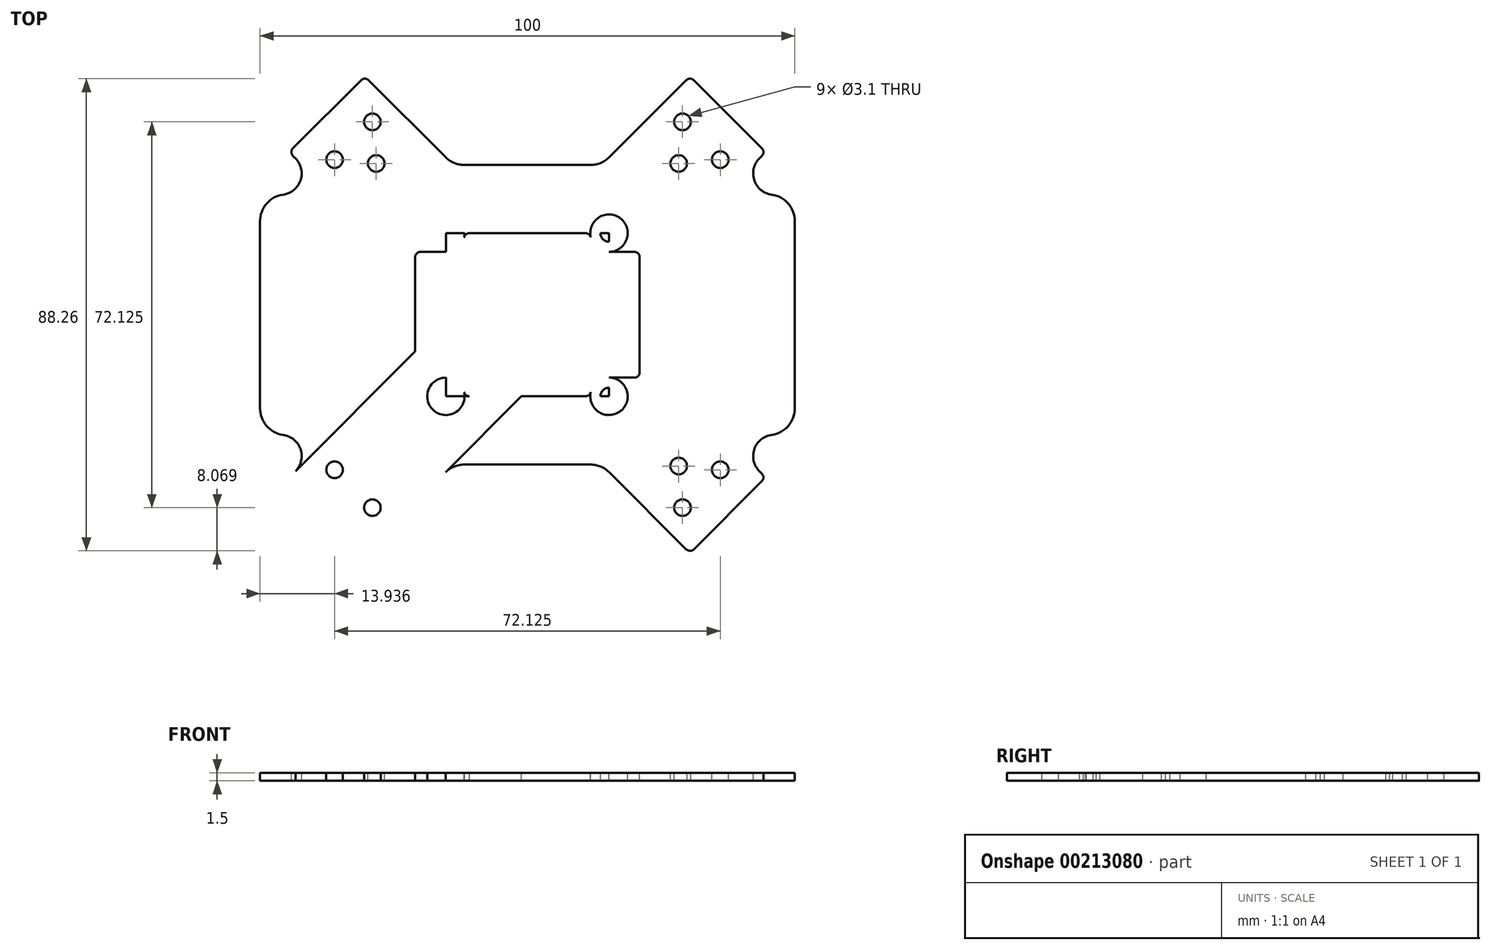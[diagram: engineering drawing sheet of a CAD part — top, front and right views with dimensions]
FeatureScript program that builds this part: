
annotation { "Feature Type Name" : "Feature", "Feature Type Description" : "" }
export const myFeature = defineFeature(function(context is Context, id is Id, definition is map)
    precondition{}
    {
        {
            var Q0;
            Q0=qCreatedBy(makeId("Top.planeOp"),FACE);
            var sketch = newSketch(context, id + "F0", { "sketchPlane" : qUnion([Q0])});
            skLineSegment(sketch, "E0", {"start": v(-118.51, 28.17) * mm, "end": v(21.49, -111.83) * mm});
            skLineSegment(sketch, "E1", {"start": v(-118.51, -111.83) * mm, "end": v(21.49, 28.17) * mm});
            skLineSegment(sketch, "E2", {"start": v(-78.21, 2.01) * mm, "end": v(-4.67, -71.53) * mm});
            skLineSegment(sketch, "E3", {"start": v(-92.35, -12.13) * mm, "end": v(-18.81, -85.67) * mm});
            skLineSegment(sketch, "E4", {"start": v(-30.13, -9.3) * mm, "end": v(-18.81, 2.01) * mm});
            skLineSegment(sketch, "E5", {"start": v(-15.99, -23.44) * mm, "end": v(-4.67, -12.13) * mm});
            skLineSegment(sketch, "E6", {"start": v(-76.51, -27.97) * mm, "end": v(-76.51, -55.69) * mm});
            skLineSegment(sketch, "E7", {"start": v(-20.51, -27.97) * mm, "end": v(-20.51, -55.69) * mm});
            skPoint(sketch, "E8", {"position": v(-48.51, -41.83) * mm});
            skCircle(sketch, "E9", {"center": v(-81.51, -30.04) * mm, "radius": 5 * mm});
            skCircle(sketch, "E10", {"center": v(-81.51, -53.62) * mm, "radius": 5 * mm});
            skCircle(sketch, "E11", {"center": v(-15.51, -30.04) * mm, "radius": 5 * mm});
            skCircle(sketch, "E12", {"center": v(-15.51, -53.62) * mm, "radius": 5 * mm});
            skLineSegment(sketch, "E13", {"start": v(-62.37, -13.83) * mm, "end": v(-34.65, -13.83) * mm});
            skLineSegment(sketch, "E14", {"start": v(-62.37, -69.83) * mm, "end": v(-34.65, -69.83) * mm});
            skCircle(sketch, "E15", {"center": v(-60.3, -74.83) * mm, "radius": 5 * mm});
            skCircle(sketch, "E16", {"center": v(-36.73, -74.83) * mm, "radius": 5 * mm});
            skLineSegment(sketch, "E17", {"start": v(-80.33, -24.15) * mm, "end": v(-66.19, -10) * mm});
            skCircle(sketch, "E18", {"center": v(-76.8, -13.54) * mm, "radius": 1.55 * mm});
            skCircle(sketch, "E19", {"center": v(-77.5, -5.77) * mm, "radius": 1.55 * mm});
            skCircle(sketch, "E20", {"center": v(-84.57, -12.84) * mm, "radius": 1.55 * mm});
            skLineSegment(sketch, "E21", {"start": v(-92.35, -10.72) * mm, "end": v(-79.62, 2.01) * mm});
            skLineSegment(sketch, "E22", {"start": v(-88.1, -16.37) * mm, "end": v(-73.97, -2.23) * mm});
            skLineSegment(sketch, "E23", {"start": v(-48.51, -27.69) * mm, "end": v(-48.51, -55.97) * mm});
            skLineSegment(sketch, "E24", {"start": v(-62.65, -41.83) * mm, "end": v(-34.37, -41.83) * mm});
            skLineSegment(sketch, "E25.MirrorCS", {"start": v(-17.4, -23.44) * mm, "end": v(-30.13, -10.72) * mm});
            skLineSegment(sketch, "E26.MirrorCS", {"start": v(-4.67, -10.72) * mm, "end": v(-17.4, 2.01) * mm});
            skLineSegment(sketch, "E27.MirrorCS", {"start": v(-8.91, -16.37) * mm, "end": v(-23.06, -2.23) * mm});
            skCircle(sketch, "E28.MirrorC", {"center": v(-19.52, -5.77) * mm, "radius": 1.55 * mm});
            skCircle(sketch, "E29.MirrorC", {"center": v(-20.23, -13.54) * mm, "radius": 1.55 * mm});
            skCircle(sketch, "E30.MirrorC", {"center": v(-12.45, -12.84) * mm, "radius": 1.55 * mm});
            skPoint(sketch, "E31.newPointB", {"position": v(-30.83, -10) * mm});
            skArc(sketch, "E31.filletArc", {"start": v(-30.13, -9.3) * mm, "mid": v(-30.42, -10) * mm, "end": v(-30.13, -10.72) * mm});
            skPoint(sketch, "E32.newPointB", {"position": v(-16.7, -24.15) * mm});
            skArc(sketch, "E32.filletArc", {"start": v(-17.4, -23.44) * mm, "mid": v(-16.7, -23.74) * mm, "end": v(-15.99, -23.44) * mm});
            skLineSegment(sketch, "E33", {"start": v(-30.13, -9.3) * mm, "end": v(-92.35, -71.53) * mm});
            skLineSegment(sketch, "E34", {"start": v(-15.99, -23.44) * mm, "end": v(-78.21, -85.67) * mm});
            skCircle(sketch, "E35.MirrorC", {"center": v(-76.8, -70.11) * mm, "radius": 1.55 * mm});
            skCircle(sketch, "E36.MirrorC", {"center": v(-77.5, -77.9) * mm, "radius": 1.55 * mm});
            skCircle(sketch, "E37.MirrorC", {"center": v(-84.57, -70.82) * mm, "radius": 1.55 * mm});
            skCircle(sketch, "E38.MirrorC", {"center": v(-20.23, -70.11) * mm, "radius": 1.55 * mm});
            skCircle(sketch, "E39.MirrorC", {"center": v(-12.45, -70.82) * mm, "radius": 1.55 * mm});
            skCircle(sketch, "E40.MirrorC", {"center": v(-19.52, -77.9) * mm, "radius": 1.55 * mm});
            skLineSegment(sketch, "E41.MirrorCS", {"start": v(-92.35, -72.94) * mm, "end": v(-79.62, -85.67) * mm});
            skLineSegment(sketch, "E42.MirrorCS", {"start": v(-4.67, -72.94) * mm, "end": v(-17.4, -85.67) * mm});
            skCircle(sketch, "E43", {"center": v(-63.76, -26.58) * mm, "radius": 1.6 * mm});
            skCircle(sketch, "E44", {"center": v(-33.26, -26.58) * mm, "radius": 1.6 * mm});
            skCircle(sketch, "E45", {"center": v(-33.26, -57.08) * mm, "radius": 1.6 * mm});
            skCircle(sketch, "E46", {"center": v(-63.76, -57.08) * mm, "radius": 1.6 * mm});
            skCircle(sketch, "E47", {"center": v(-63.76, -26.58) * mm, "radius": 3.5 * mm});
            skCircle(sketch, "E48", {"center": v(-33.26, -26.58) * mm, "radius": 3.5 * mm});
            skCircle(sketch, "E49", {"center": v(-33.26, -57.08) * mm, "radius": 3.5 * mm});
            skCircle(sketch, "E50", {"center": v(-63.76, -57.08) * mm, "radius": 3.5 * mm});
            skLineSegment(sketch, "E51", {"start": v(-33.26, -26.58) * mm, "end": v(-33.26, -57.08) * mm});
            skLineSegment(sketch, "E52", {"start": v(-33.26, -57.08) * mm, "end": v(-63.76, -57.08) * mm});
            skLineSegment(sketch, "E53", {"start": v(-63.76, -57.08) * mm, "end": v(-63.76, -26.58) * mm});
            skLineSegment(sketch, "E54", {"start": v(-63.76, -26.58) * mm, "end": v(-33.26, -26.58) * mm});
            skPoint(sketch, "E55.newPointB", {"position": v(-97.08, -15.45) * mm});
            skArc(sketch, "E55.filletArc", {"start": v(-78.21, 2.01) * mm, "mid": v(-78.92, 2.3) * mm, "end": v(-79.62, 2.01) * mm});
            skPoint(sketch, "E56.newPointA", {"position": v(-111.23, -29.59) * mm});
            skArc(sketch, "E56.filletArc", {"start": v(-92.35, -10.72) * mm, "mid": v(-92.65, -11.42) * mm, "end": v(-92.35, -12.13) * mm});
            skPoint(sketch, "E57.newPointB", {"position": v(0.06, -15.45) * mm});
            skArc(sketch, "E57.filletArc", {"start": v(-17.4, 2.01) * mm, "mid": v(-18.1, 2.3) * mm, "end": v(-18.81, 2.01) * mm});
            skPoint(sketch, "E58.newPointA", {"position": v(14.2, -29.59) * mm});
            skArc(sketch, "E58.filletArc", {"start": v(-4.67, -12.13) * mm, "mid": v(-4.38, -11.42) * mm, "end": v(-4.67, -10.72) * mm});
            skPoint(sketch, "E59.newPointB", {"position": v(14.2, -54.07) * mm});
            skArc(sketch, "E59.filletArc", {"start": v(-4.67, -72.94) * mm, "mid": v(-4.38, -72.23) * mm, "end": v(-4.67, -71.53) * mm});
            skPoint(sketch, "E60.newPointA", {"position": v(0.06, -68.21) * mm});
            skArc(sketch, "E60.filletArc", {"start": v(-18.81, -85.67) * mm, "mid": v(-18.1, -85.96) * mm, "end": v(-17.4, -85.67) * mm});
            skPoint(sketch, "E61.newPointB", {"position": v(-97.08, -68.21) * mm});
            skArc(sketch, "E61.filletArc", {"start": v(-79.62, -85.67) * mm, "mid": v(-78.92, -85.96) * mm, "end": v(-78.21, -85.67) * mm});
            skPoint(sketch, "E62.newPointA", {"position": v(-111.23, -54.07) * mm});
            skArc(sketch, "E62.filletArc", {"start": v(-92.35, -71.53) * mm, "mid": v(-92.65, -72.23) * mm, "end": v(-92.35, -72.94) * mm});
            skLineSegment(sketch, "E63", {"start": v(-63.76, -30.08) * mm, "end": v(-68.51, -30.08) * mm});
            skLineSegment(sketch, "E64", {"start": v(-69.51, -31.08) * mm, "end": v(-69.51, -52.58) * mm});
            skLineSegment(sketch, "E65", {"start": v(-68.51, -53.58) * mm, "end": v(-63.76, -53.58) * mm});
            skPoint(sketch, "E66.visualSharp", {"position": v(-69.51, -30.08) * mm});
            skArc(sketch, "E66.filletArc", {"start": v(-68.51, -30.08) * mm, "mid": v(-69.22, -30.37) * mm, "end": v(-69.51, -31.08) * mm});
            skPoint(sketch, "E67.visualSharp", {"position": v(-69.51, -53.58) * mm});
            skArc(sketch, "E67.filletArc", {"start": v(-69.51, -52.58) * mm, "mid": v(-69.22, -53.29) * mm, "end": v(-68.51, -53.58) * mm});
            skLineSegment(sketch, "E68.MirrorCS", {"start": v(-33.26, -30.08) * mm, "end": v(-28.51, -30.08) * mm});
            skArc(sketch, "E69.MirrorCS", {"start": v(-28.51, -30.08) * mm, "mid": v(-27.8, -30.37) * mm, "end": v(-27.51, -31.08) * mm});
            skLineSegment(sketch, "E70.MirrorCS", {"start": v(-27.51, -31.08) * mm, "end": v(-27.51, -52.58) * mm});
            skArc(sketch, "E71.MirrorCS", {"start": v(-27.51, -52.58) * mm, "mid": v(-27.8, -53.29) * mm, "end": v(-28.51, -53.58) * mm});
            skLineSegment(sketch, "E72.MirrorCS", {"start": v(-28.51, -53.58) * mm, "end": v(-33.26, -53.58) * mm});
            skCircle(sketch, "E73", {"center": v(-59.37, -56.08) * mm, "radius": 1 * mm});
            skCircle(sketch, "E74", {"center": v(-37.65, -56.08) * mm, "radius": 1 * mm});
            skCircle(sketch, "E75.MirrorC", {"center": v(-59.37, -27.58) * mm, "radius": 1 * mm});
            skCircle(sketch, "E76.MirrorC", {"center": v(-37.65, -27.58) * mm, "radius": 1 * mm});
            skPoint(sketch, "E77.MirrorP", {"position": v(-63.84, -61.83) * mm});
            skPoint(sketch, "E78.MirrorP", {"position": v(-72.84, -61.83) * mm});
            skLineSegment(sketch, "E79.MirrorCS", {"start": v(-63.84, -62.83) * mm, "end": v(-63.84, -62.83) * mm});
            skPoint(sketch, "E80.MirrorP", {"position": v(-63.84, -63.83) * mm});
            skPoint(sketch, "E81.centerSnap0", {"position": v(-48.51, -26.58) * mm});
            skLineSegment(sketch, "E82", {"start": v(-11.87, -19.33) * mm, "end": v(-3.51, -19.33) * mm});
            skLineSegment(sketch, "E83", {"start": v(1.49, -24.33) * mm, "end": v(1.49, -59.33) * mm});
            skLineSegment(sketch, "E84", {"start": v(-3.51, -64.33) * mm, "end": v(-11.87, -64.33) * mm});
            skLineSegment(sketch, "E85", {"start": v(-85.15, -64.33) * mm, "end": v(-93.51, -64.33) * mm});
            skLineSegment(sketch, "E86", {"start": v(-98.51, -59.33) * mm, "end": v(-98.51, -24.33) * mm});
            skLineSegment(sketch, "E87", {"start": v(-93.51, -19.33) * mm, "end": v(-85.15, -19.33) * mm});
            skCircle(sketch, "E88", {"center": v(-94.73, -15.41) * mm, "radius": 4 * mm});
            skCircle(sketch, "E89.MirrorC", {"center": v(-94.73, -68.25) * mm, "radius": 4 * mm});
            skCircle(sketch, "E90.MirrorC", {"center": v(-2.3, -68.25) * mm, "radius": 4 * mm});
            skCircle(sketch, "E91.MirrorC", {"center": v(-2.3, -15.41) * mm, "radius": 4 * mm});
            skCircle(sketch, "E92.MirrorC", {"center": v(-36.73, -8.83) * mm, "radius": 5 * mm});
            skCircle(sketch, "E93.MirrorC", {"center": v(-60.3, -8.83) * mm, "radius": 5 * mm});
            skPoint(sketch, "E94.visualSharp", {"position": v(-98.51, -19.33) * mm});
            skArc(sketch, "E94.filletArc", {"start": v(-93.51, -19.33) * mm, "mid": v(-97.05, -20.8) * mm, "end": v(-98.51, -24.33) * mm});
            skPoint(sketch, "E95.visualSharp", {"position": v(-98.51, -64.33) * mm});
            skArc(sketch, "E95.filletArc", {"start": v(-98.51, -59.33) * mm, "mid": v(-97.05, -62.86) * mm, "end": v(-93.51, -64.33) * mm});
            skPoint(sketch, "E96.visualSharp", {"position": v(1.49, -19.33) * mm});
            skArc(sketch, "E96.filletArc", {"start": v(1.49, -24.33) * mm, "mid": v(0.02, -20.8) * mm, "end": v(-3.51, -19.33) * mm});
            skPoint(sketch, "E97.visualSharp", {"position": v(1.49, -64.33) * mm});
            skArc(sketch, "E97.filletArc", {"start": v(-3.51, -64.33) * mm, "mid": v(0.02, -62.86) * mm, "end": v(1.49, -59.33) * mm});
            skSolve(sketch);
        }
        {
            var Q0;
            {var subQ0=sQuery(id+"F0.wireOp",EDGE,"E34");var subQ1=sQuery(id+"F0.wireOp",EDGE,"E7");var subQ2=makeQuery(id+"F0.imprint","INTERSECT",VERTEX,{"derivedFrom":[subQ1,subQ0]});Q0=makeQuery(id+"F0.imprint","IMPRINT",FACE,{"disambiguationData":[TD([[makeQuery(id+"F0.imprint","IMPRINT",EDGE,{"disambiguationData":[TD([[subQ2,-1.0]])],"derivedFrom":subQ1}),1.0]])]});}
            var Q1;
            {var subQ0=sQuery(id+"F0.wireOp",EDGE,"E34");var subQ1=sQuery(id+"F0.wireOp",EDGE,"E14");var subQ2=makeQuery(id+"F0.imprint","INTERSECT",VERTEX,{"derivedFrom":[subQ1,subQ0]});Q1=makeQuery(id+"F0.imprint","IMPRINT",FACE,{"disambiguationData":[TD([[makeQuery(id+"F0.imprint","IMPRINT",EDGE,{"disambiguationData":[TD([[subQ2,-1.0]])],"derivedFrom":subQ1}),-1.0]])]});}
            var Q2;
            {var subQ1=sQuery(id+"F0.wireOp",EDGE,"E6");var subQ5=sQuery(id+"F0.wireOp",EDGE,"E3");var subQ6=makeQuery(id+"F0.imprint","INTERSECT",VERTEX,{"derivedFrom":[subQ5,subQ1]});Q2=makeQuery(id+"F0.imprint","IMPRINT",FACE,{"disambiguationData":[TD([[makeQuery(id+"F0.imprint","IMPRINT",EDGE,{"disambiguationData":[TD([[subQ6,-1.0]])],"derivedFrom":subQ5}),-1.0]])]});}
            var Q3;
            {var subQ0=sQuery(id+"F0.wireOp",EDGE,"E6");var subQ1=sQuery(id+"F0.wireOp",EDGE,"E3");var subQ2=makeQuery(id+"F0.imprint","INTERSECT",VERTEX,{"derivedFrom":[subQ1,subQ0]});Q3=makeQuery(id+"F0.imprint","IMPRINT",FACE,{"disambiguationData":[TD([[makeQuery(id+"F0.imprint","IMPRINT",EDGE,{"disambiguationData":[TD([[subQ2,1.0]])],"derivedFrom":subQ1}),-1.0]])]});}
            var Q4;
            {var subQ0=sQuery(id+"F0.wireOp",EDGE,"E7");var subQ5=sQuery(id+"F0.wireOp",EDGE,"E2");var subQ6=makeQuery(id+"F0.imprint","INTERSECT",VERTEX,{"derivedFrom":[subQ5,subQ0]});Q4=makeQuery(id+"F0.imprint","IMPRINT",FACE,{"disambiguationData":[TD([[makeQuery(id+"F0.imprint","IMPRINT",EDGE,{"disambiguationData":[TD([[subQ6,1.0]])],"derivedFrom":subQ5}),1.0]])]});}
            var Q5;
            {var subQ0=sQuery(id+"F0.wireOp",EDGE,"E7");var subQ1=sQuery(id+"F0.wireOp",EDGE,"E2");var subQ2=makeQuery(id+"F0.imprint","INTERSECT",VERTEX,{"derivedFrom":[subQ1,subQ0]});Q5=makeQuery(id+"F0.imprint","IMPRINT",FACE,{"disambiguationData":[TD([[makeQuery(id+"F0.imprint","IMPRINT",EDGE,{"disambiguationData":[TD([[subQ2,-1.0]])],"derivedFrom":subQ1}),1.0]])]});}
            var Q6;
            {var subQ0=sQuery(id+"F0.wireOp",EDGE,"E13");Q6=makeQuery(id+"F0.imprint","IMPRINT",FACE,{"disambiguationData":[TD([[makeQuery(id+"F0.imprint","IMPRINT",EDGE,{"derivedFrom":subQ0}),-1.0]])]});}
            var Q7;
            {var subQ0=sQuery(id+"F0.wireOp",EDGE,"E14");var subQ1=sQuery(id+"F0.wireOp",EDGE,"E3");var subQ2=makeQuery(id+"F0.imprint","INTERSECT",VERTEX,{"derivedFrom":[subQ1,subQ0]});Q7=makeQuery(id+"F0.imprint","IMPRINT",FACE,{"disambiguationData":[TD([[makeQuery(id+"F0.imprint","IMPRINT",EDGE,{"disambiguationData":[TD([[subQ2,1.0]])],"derivedFrom":subQ1}),-1.0]])]});}
            var Q8;
            {var subQ0=sQuery(id+"F0.wireOp",EDGE,"E14");var subQ1=sQuery(id+"F0.wireOp",EDGE,"E3");var subQ2=makeQuery(id+"F0.imprint","INTERSECT",VERTEX,{"derivedFrom":[subQ1,subQ0]});Q8=makeQuery(id+"F0.imprint","IMPRINT",FACE,{"disambiguationData":[TD([[makeQuery(id+"F0.imprint","IMPRINT",EDGE,{"disambiguationData":[TD([[subQ2,-1.0]])],"derivedFrom":subQ1}),-1.0]])]});}
            var Q9;
            {var subQ4=sQuery(id+"F0.wireOp",EDGE,"E22");var subQ7=sQuery(id+"F0.wireOp",EDGE,"E0");var subQ10=makeQuery(id+"F0.imprint","INTERSECT",VERTEX,{"derivedFrom":[subQ7,subQ4]});Q9=makeQuery(id+"F0.imprint","IMPRINT",FACE,{"disambiguationData":[TD([[makeQuery(id+"F0.imprint","IMPRINT",EDGE,{"disambiguationData":[TD([[subQ10,-1.0]])],"derivedFrom":subQ7}),-1.0]])]});}
            var Q10;
            {var subQ11=sQuery(id+"F0.wireOp",EDGE,"E56.filletArc");Q10=makeQuery(id+"F0.imprint","IMPRINT",FACE,{"disambiguationData":[TD([[makeQuery(id+"F0.imprint","IMPRINT",EDGE,{"derivedFrom":subQ11}),1.0]])]});}
            var Q11;
            {var subQ0=sQuery(id+"F0.wireOp",EDGE,"E55.filletArc");Q11=makeQuery(id+"F0.imprint","IMPRINT",FACE,{"disambiguationData":[TD([[makeQuery(id+"F0.imprint","IMPRINT",EDGE,{"derivedFrom":subQ0}),1.0]])]});}
            var Q12;
            {var subQ3=sQuery(id+"F0.wireOp",EDGE,"E22");var subQ6=sQuery(id+"F0.wireOp",EDGE,"E0");var subQ9=makeQuery(id+"F0.imprint","INTERSECT",VERTEX,{"derivedFrom":[subQ6,subQ3]});Q12=makeQuery(id+"F0.imprint","IMPRINT",FACE,{"disambiguationData":[TD([[makeQuery(id+"F0.imprint","IMPRINT",EDGE,{"disambiguationData":[TD([[subQ9,-1.0]])],"derivedFrom":subQ6}),1.0]])]});}
            var Q13;
            {var subQ0=sQuery(id+"F0.wireOp",EDGE,"E17");var subQ3=sQuery(id+"F0.wireOp",EDGE,"E0");var subQ4=makeQuery(id+"F0.imprint","INTERSECT",VERTEX,{"derivedFrom":[subQ3,subQ0]});Q13=makeQuery(id+"F0.imprint","IMPRINT",FACE,{"disambiguationData":[TD([[makeQuery(id+"F0.imprint","IMPRINT",EDGE,{"disambiguationData":[TD([[subQ4,-1.0]])],"derivedFrom":subQ3}),1.0]])]});}
            var Q14;
            {var subQ4=sQuery(id+"F0.wireOp",EDGE,"E63");Q14=makeQuery(id+"F0.imprint","IMPRINT",FACE,{"disambiguationData":[TD([[makeQuery(id+"F0.imprint","IMPRINT",EDGE,{"derivedFrom":subQ4}),-1.0]])]});}
            var Q15;
            {var subQ0=sQuery(id+"F0.wireOp",EDGE,"E31.filletArc");Q15=makeQuery(id+"F0.imprint","IMPRINT",FACE,{"disambiguationData":[TD([[makeQuery(id+"F0.imprint","IMPRINT",EDGE,{"derivedFrom":subQ0}),1.0]])]});}
            var Q16;
            {var subQ5=sQuery(id+"F0.wireOp",EDGE,"E57.filletArc");Q16=makeQuery(id+"F0.imprint","IMPRINT",FACE,{"disambiguationData":[TD([[makeQuery(id+"F0.imprint","IMPRINT",EDGE,{"derivedFrom":subQ5}),1.0]])]});}
            var Q17;
            {var subQ0=sQuery(id+"F0.wireOp",EDGE,"E58.filletArc");Q17=makeQuery(id+"F0.imprint","IMPRINT",FACE,{"disambiguationData":[TD([[makeQuery(id+"F0.imprint","IMPRINT",EDGE,{"derivedFrom":subQ0}),1.0]])]});}
            var Q18;
            {var subQ4=sQuery(id+"F0.wireOp",EDGE,"E32.filletArc");Q18=makeQuery(id+"F0.imprint","IMPRINT",FACE,{"disambiguationData":[TD([[makeQuery(id+"F0.imprint","IMPRINT",EDGE,{"derivedFrom":subQ4}),1.0]])]});}
            var Q19;
            {var subQ1=sQuery(id+"F0.wireOp",EDGE,"E31.filletArc");Q19=makeQuery(id+"F0.imprint","IMPRINT",FACE,{"disambiguationData":[TD([[makeQuery(id+"F0.imprint","IMPRINT",EDGE,{"derivedFrom":subQ1}),-1.0]])]});}
            var Q20;
            {var subQ1=sQuery(id+"F0.wireOp",EDGE,"E32.filletArc");Q20=makeQuery(id+"F0.imprint","IMPRINT",FACE,{"disambiguationData":[TD([[makeQuery(id+"F0.imprint","IMPRINT",EDGE,{"derivedFrom":subQ1}),-1.0]])]});}
            var Q21;
            Q21=makeQuery(id+"F0.imprint","IMPRINT",FACE,{"disambiguationData":[TD([[makeQuery(id+"F0.imprint","IMPRINT",EDGE,{"derivedFrom":sQuery(id+"F0.wireOp",EDGE,"E39.MirrorC")}),-1.0]])]});
            var Q22;
            Q22=makeQuery(id+"F0.imprint","IMPRINT",FACE,{"disambiguationData":[TD([[makeQuery(id+"F0.imprint","IMPRINT",EDGE,{"derivedFrom":sQuery(id+"F0.wireOp",EDGE,"E40.MirrorC")}),-1.0]])]});
            var Q23;
            Q23=makeQuery(id+"F0.imprint","IMPRINT",FACE,{"disambiguationData":[TD([[makeQuery(id+"F0.imprint","IMPRINT",EDGE,{"derivedFrom":sQuery(id+"F0.wireOp",EDGE,"E36.MirrorC")}),1.0]])]});
            var Q24;
            Q24=makeQuery(id+"F0.imprint","IMPRINT",FACE,{"disambiguationData":[TD([[makeQuery(id+"F0.imprint","IMPRINT",EDGE,{"derivedFrom":sQuery(id+"F0.wireOp",EDGE,"E37.MirrorC")}),1.0]])]});
            var Q25;
            {var subQ0=sQuery(id+"F0.wireOp",EDGE,"E47");var subQ1=sQuery(id+"F0.wireOp",EDGE,"E0");var subQ2=makeQuery(id+"F0.imprint","INTERSECT",VERTEX,{"disambiguationData":[OD(0.0)],"derivedFrom":[subQ1,subQ0]});Q25=makeQuery(id+"F0.imprint","IMPRINT",FACE,{"disambiguationData":[TD([[makeQuery(id+"F0.imprint","IMPRINT",EDGE,{"disambiguationData":[TD([[subQ2,-1.0]])],"derivedFrom":subQ1}),-1.0]])]});}
            var Q26;
            {var subQ0=sQuery(id+"F0.wireOp",EDGE,"E47");var subQ1=sQuery(id+"F0.wireOp",EDGE,"E0");var subQ2=makeQuery(id+"F0.imprint","INTERSECT",VERTEX,{"disambiguationData":[OD(0.0)],"derivedFrom":[subQ1,subQ0]});Q26=makeQuery(id+"F0.imprint","IMPRINT",FACE,{"disambiguationData":[TD([[makeQuery(id+"F0.imprint","IMPRINT",EDGE,{"disambiguationData":[TD([[subQ2,-1.0]])],"derivedFrom":subQ1}),1.0]])]});}
            var Q27;
            {var subQ4=sQuery(id+"F0.wireOp",EDGE,"E0");var subQ6=sQuery(id+"F0.wireOp",EDGE,"E43");var subQ7=makeQuery(id+"F0.imprint","INTERSECT",VERTEX,{"disambiguationData":[OD(1.0)],"derivedFrom":[subQ4,subQ6]});Q27=makeQuery(id+"F0.imprint","IMPRINT",FACE,{"disambiguationData":[TD([[makeQuery(id+"F0.imprint","IMPRINT",EDGE,{"disambiguationData":[TD([[subQ7,-1.0]])],"derivedFrom":subQ4}),1.0]])]});}
            var Q28;
            {var subQ0=sQuery(id+"F0.wireOp",EDGE,"E43");var subQ1=sQuery(id+"F0.wireOp",EDGE,"E0");var subQ2=makeQuery(id+"F0.imprint","INTERSECT",VERTEX,{"disambiguationData":[OD(1.0)],"derivedFrom":[subQ1,subQ0]});Q28=makeQuery(id+"F0.imprint","IMPRINT",FACE,{"disambiguationData":[TD([[makeQuery(id+"F0.imprint","IMPRINT",EDGE,{"disambiguationData":[TD([[subQ2,-1.0]])],"derivedFrom":subQ1}),-1.0]])]});}
            var Q29;
            {var subQ0=sQuery(id+"F0.wireOp",EDGE,"E48");var subQ1=sQuery(id+"F0.wireOp",EDGE,"E1");var subQ2=makeQuery(id+"F0.imprint","INTERSECT",VERTEX,{"disambiguationData":[OD(0.0)],"derivedFrom":[subQ1,subQ0]});Q29=makeQuery(id+"F0.imprint","IMPRINT",FACE,{"disambiguationData":[TD([[makeQuery(id+"F0.imprint","IMPRINT",EDGE,{"disambiguationData":[TD([[subQ2,-1.0]])],"derivedFrom":subQ1}),1.0]])]});}
            var Q30;
            {var subQ0=sQuery(id+"F0.wireOp",EDGE,"E48");var subQ1=sQuery(id+"F0.wireOp",EDGE,"E1");var subQ2=makeQuery(id+"F0.imprint","INTERSECT",VERTEX,{"disambiguationData":[OD(0.0)],"derivedFrom":[subQ1,subQ0]});Q30=makeQuery(id+"F0.imprint","IMPRINT",FACE,{"disambiguationData":[TD([[makeQuery(id+"F0.imprint","IMPRINT",EDGE,{"disambiguationData":[TD([[subQ2,-1.0]])],"derivedFrom":subQ1}),-1.0]])]});}
            var Q31;
            {var subQ0=sQuery(id+"F0.wireOp",EDGE,"E44");var subQ1=sQuery(id+"F0.wireOp",EDGE,"E1");var subQ2=makeQuery(id+"F0.imprint","INTERSECT",VERTEX,{"disambiguationData":[OD(1.0)],"derivedFrom":[subQ1,subQ0]});Q31=makeQuery(id+"F0.imprint","IMPRINT",FACE,{"disambiguationData":[TD([[makeQuery(id+"F0.imprint","IMPRINT",EDGE,{"disambiguationData":[TD([[subQ2,-1.0]])],"derivedFrom":subQ1}),-1.0]])]});}
            var Q32;
            {var subQ0=sQuery(id+"F0.wireOp",EDGE,"E44");var subQ1=sQuery(id+"F0.wireOp",EDGE,"E1");var subQ2=makeQuery(id+"F0.imprint","INTERSECT",VERTEX,{"disambiguationData":[OD(1.0)],"derivedFrom":[subQ1,subQ0]});Q32=makeQuery(id+"F0.imprint","IMPRINT",FACE,{"disambiguationData":[TD([[makeQuery(id+"F0.imprint","IMPRINT",EDGE,{"disambiguationData":[TD([[subQ2,-1.0]])],"derivedFrom":subQ1}),1.0]])]});}
            var Q33;
            {var subQ1=sQuery(id+"F0.wireOp",EDGE,"E0");var subQ5=sQuery(id+"F0.wireOp",EDGE,"E49");var subQ6=makeQuery(id+"F0.imprint","INTERSECT",VERTEX,{"disambiguationData":[OD(0.0)],"derivedFrom":[subQ1,subQ5]});Q33=makeQuery(id+"F0.imprint","IMPRINT",FACE,{"disambiguationData":[TD([[makeQuery(id+"F0.imprint","IMPRINT",EDGE,{"disambiguationData":[TD([[subQ6,-1.0]])],"derivedFrom":subQ1}),-1.0]])]});}
            var Q34;
            {var subQ0=sQuery(id+"F0.wireOp",EDGE,"E49");var subQ1=sQuery(id+"F0.wireOp",EDGE,"E0");var subQ2=makeQuery(id+"F0.imprint","INTERSECT",VERTEX,{"disambiguationData":[OD(0.0)],"derivedFrom":[subQ1,subQ0]});Q34=makeQuery(id+"F0.imprint","IMPRINT",FACE,{"disambiguationData":[TD([[makeQuery(id+"F0.imprint","IMPRINT",EDGE,{"disambiguationData":[TD([[subQ2,-1.0]])],"derivedFrom":subQ1}),1.0]])]});}
            var Q35;
            {var subQ0=sQuery(id+"F0.wireOp",EDGE,"E45");var subQ1=sQuery(id+"F0.wireOp",EDGE,"E0");var subQ2=makeQuery(id+"F0.imprint","INTERSECT",VERTEX,{"disambiguationData":[OD(1.0)],"derivedFrom":[subQ1,subQ0]});Q35=makeQuery(id+"F0.imprint","IMPRINT",FACE,{"disambiguationData":[TD([[makeQuery(id+"F0.imprint","IMPRINT",EDGE,{"disambiguationData":[TD([[subQ2,-1.0]])],"derivedFrom":subQ1}),1.0]])]});}
            var Q36;
            {var subQ0=sQuery(id+"F0.wireOp",EDGE,"E45");var subQ1=sQuery(id+"F0.wireOp",EDGE,"E0");var subQ2=makeQuery(id+"F0.imprint","INTERSECT",VERTEX,{"disambiguationData":[OD(1.0)],"derivedFrom":[subQ1,subQ0]});Q36=makeQuery(id+"F0.imprint","IMPRINT",FACE,{"disambiguationData":[TD([[makeQuery(id+"F0.imprint","IMPRINT",EDGE,{"disambiguationData":[TD([[subQ2,-1.0]])],"derivedFrom":subQ1}),-1.0]])]});}
            var Q37;
            {var subQ0=sQuery(id+"F0.wireOp",EDGE,"E50");var subQ1=sQuery(id+"F0.wireOp",EDGE,"E1");var subQ2=makeQuery(id+"F0.imprint","INTERSECT",VERTEX,{"disambiguationData":[OD(0.0)],"derivedFrom":[subQ1,subQ0]});Q37=makeQuery(id+"F0.imprint","IMPRINT",FACE,{"disambiguationData":[TD([[makeQuery(id+"F0.imprint","IMPRINT",EDGE,{"disambiguationData":[TD([[subQ2,-1.0]])],"derivedFrom":subQ1}),-1.0]])]});}
            var Q38;
            {var subQ0=sQuery(id+"F0.wireOp",EDGE,"E50");var subQ1=sQuery(id+"F0.wireOp",EDGE,"E1");var subQ2=makeQuery(id+"F0.imprint","INTERSECT",VERTEX,{"disambiguationData":[OD(0.0)],"derivedFrom":[subQ1,subQ0]});Q38=makeQuery(id+"F0.imprint","IMPRINT",FACE,{"disambiguationData":[TD([[makeQuery(id+"F0.imprint","IMPRINT",EDGE,{"disambiguationData":[TD([[subQ2,-1.0]])],"derivedFrom":subQ1}),1.0]])]});}
            var Q39;
            {var subQ0=sQuery(id+"F0.wireOp",EDGE,"E46");var subQ1=sQuery(id+"F0.wireOp",EDGE,"E1");var subQ2=makeQuery(id+"F0.imprint","INTERSECT",VERTEX,{"disambiguationData":[OD(1.0)],"derivedFrom":[subQ1,subQ0]});Q39=makeQuery(id+"F0.imprint","IMPRINT",FACE,{"disambiguationData":[TD([[makeQuery(id+"F0.imprint","IMPRINT",EDGE,{"disambiguationData":[TD([[subQ2,-1.0]])],"derivedFrom":subQ1}),1.0]])]});}
            var Q40;
            {var subQ0=sQuery(id+"F0.wireOp",EDGE,"E46");var subQ1=sQuery(id+"F0.wireOp",EDGE,"E1");var subQ2=makeQuery(id+"F0.imprint","INTERSECT",VERTEX,{"disambiguationData":[OD(1.0)],"derivedFrom":[subQ1,subQ0]});Q40=makeQuery(id+"F0.imprint","IMPRINT",FACE,{"disambiguationData":[TD([[makeQuery(id+"F0.imprint","IMPRINT",EDGE,{"disambiguationData":[TD([[subQ2,-1.0]])],"derivedFrom":subQ1}),-1.0]])]});}
            var Q41;
            {var subQ0=sQuery(id+"F0.wireOp",EDGE,"E34");var subQ1=sQuery(id+"F0.wireOp",EDGE,"E7");var subQ2=makeQuery(id+"F0.imprint","INTERSECT",VERTEX,{"derivedFrom":[subQ1,subQ0]});Q41=makeQuery(id+"F0.imprint","IMPRINT",FACE,{"disambiguationData":[TD([[makeQuery(id+"F0.imprint","IMPRINT",EDGE,{"disambiguationData":[TD([[subQ2,-1.0]])],"derivedFrom":subQ1}),1.0]])]});}
            var Q42;
            {var subQ0=sQuery(id+"F0.wireOp",EDGE,"E33");var subQ1=sQuery(id+"F0.wireOp",EDGE,"E6");var subQ2=makeQuery(id+"F0.imprint","INTERSECT",VERTEX,{"derivedFrom":[subQ1,subQ0]});Q42=makeQuery(id+"F0.imprint","IMPRINT",FACE,{"disambiguationData":[TD([[makeQuery(id+"F0.imprint","IMPRINT",EDGE,{"disambiguationData":[TD([[subQ2,1.0]])],"derivedFrom":subQ1}),-1.0]])]});}
            var Q43;
            {var subQ0=sQuery(id+"F0.wireOp",EDGE,"E34");var subQ1=sQuery(id+"F0.wireOp",EDGE,"E14");var subQ2=makeQuery(id+"F0.imprint","INTERSECT",VERTEX,{"derivedFrom":[subQ1,subQ0]});Q43=makeQuery(id+"F0.imprint","IMPRINT",FACE,{"disambiguationData":[TD([[makeQuery(id+"F0.imprint","IMPRINT",EDGE,{"disambiguationData":[TD([[subQ2,-1.0]])],"derivedFrom":subQ1}),-1.0]])]});}
            var Q44;
            {var subQ0=sQuery(id+"F0.wireOp",EDGE,"E54");var subQ1=sQuery(id+"F0.wireOp",EDGE,"E47");var subQ2=makeQuery(id+"F0.imprint","INTERSECT",VERTEX,{"derivedFrom":[subQ1,subQ0]});Q44=makeQuery(id+"F0.imprint","IMPRINT",FACE,{"disambiguationData":[TD([[makeQuery(id+"F0.imprint","IMPRINT",EDGE,{"disambiguationData":[TD([[subQ2,1.0]])],"derivedFrom":subQ1}),-1.0]])]});}
            var Q45;
            {var subQ0=sQuery(id+"F0.wireOp",EDGE,"E54");var subQ1=sQuery(id+"F0.wireOp",EDGE,"E48");var subQ2=makeQuery(id+"F0.imprint","INTERSECT",VERTEX,{"derivedFrom":[subQ1,subQ0]});Q45=makeQuery(id+"F0.imprint","IMPRINT",FACE,{"disambiguationData":[TD([[makeQuery(id+"F0.imprint","IMPRINT",EDGE,{"disambiguationData":[TD([[subQ2,-1.0]])],"derivedFrom":subQ1}),-1.0]])]});}
            var Q46;
            {var subQ0=sQuery(id+"F0.wireOp",EDGE,"E74");var subQ1=sQuery(id+"F0.wireOp",EDGE,"E49");var subQ2=makeQuery(id+"F0.imprint","INTERSECT",VERTEX,{"derivedFrom":[subQ1,subQ0]});Q46=makeQuery(id+"F0.imprint","IMPRINT",FACE,{"disambiguationData":[TD([[makeQuery(id+"F0.imprint","IMPRINT",EDGE,{"disambiguationData":[TD([[subQ2,-1.0]])],"derivedFrom":subQ1}),-1.0]])]});}
            var Q47;
            {var subQ0=sQuery(id+"F0.wireOp",EDGE,"E73");var subQ1=sQuery(id+"F0.wireOp",EDGE,"E50");var subQ2=makeQuery(id+"F0.imprint","INTERSECT",VERTEX,{"derivedFrom":[subQ1,subQ0]});Q47=makeQuery(id+"F0.imprint","IMPRINT",FACE,{"disambiguationData":[TD([[makeQuery(id+"F0.imprint","IMPRINT",EDGE,{"disambiguationData":[TD([[subQ2,1.0]])],"derivedFrom":subQ1}),-1.0]])]});}
            var Q48;
            {var subQ0=sQuery(id+"F0.wireOp",EDGE,"E3");var subQ1=makeQuery(id+"F0.imprint","INTERSECT",VERTEX,{"derivedFrom":[subQ0,sQuery(id+"F0.wireOp",EDGE,"E22")]});Q48=makeQuery(id+"F0.imprint","IMPRINT",FACE,{"disambiguationData":[TD([[makeQuery(id+"F0.imprint","IMPRINT",EDGE,{"disambiguationData":[TD([[subQ1,1.0]])],"derivedFrom":subQ0}),-1.0]])]});}
            var Q49;
            {var subQ1=sQuery(id+"F0.wireOp",EDGE,"E86");Q49=makeQuery(id+"F0.imprint","IMPRINT",FACE,{"disambiguationData":[TD([[makeQuery(id+"F0.imprint","IMPRINT",EDGE,{"derivedFrom":subQ1}),-1.0]])]});}
            var Q50;
            {var subQ0=sQuery(id+"F0.wireOp",EDGE,"E10");var subQ1=makeQuery(id+"F0.imprint","INTERSECT",VERTEX,{"derivedFrom":[sQuery(id+"F0.wireOp",EDGE,"E6"),subQ0]});Q50=makeQuery(id+"F0.imprint","IMPRINT",FACE,{"disambiguationData":[TD([[makeQuery(id+"F0.imprint","IMPRINT",EDGE,{"disambiguationData":[TD([[subQ1,-1.0]])],"derivedFrom":subQ0}),1.0]])]});}
            var Q51;
            {var subQ0=sQuery(id+"F0.wireOp",EDGE,"E9");var subQ1=makeQuery(id+"F0.imprint","INTERSECT",VERTEX,{"derivedFrom":[sQuery(id+"F0.wireOp",EDGE,"E3"),subQ0]});Q51=makeQuery(id+"F0.imprint","IMPRINT",FACE,{"disambiguationData":[TD([[makeQuery(id+"F0.imprint","IMPRINT",EDGE,{"disambiguationData":[TD([[subQ1,1.0]])],"derivedFrom":subQ0}),1.0]])]});}
            var Q52;
            {var subQ0=sQuery(id+"F0.wireOp",EDGE,"E83");Q52=makeQuery(id+"F0.imprint","IMPRINT",FACE,{"disambiguationData":[TD([[makeQuery(id+"F0.imprint","IMPRINT",EDGE,{"derivedFrom":subQ0}),-1.0]])]});}
            var Q53;
            {var subQ0=sQuery(id+"F0.wireOp",EDGE,"E11");var subQ1=makeQuery(id+"F0.imprint","INTERSECT",VERTEX,{"derivedFrom":[sQuery(id+"F0.wireOp",EDGE,"E7"),subQ0]});Q53=makeQuery(id+"F0.imprint","IMPRINT",FACE,{"disambiguationData":[TD([[makeQuery(id+"F0.imprint","IMPRINT",EDGE,{"disambiguationData":[TD([[subQ1,1.0]])],"derivedFrom":subQ0}),1.0]])]});}
            var Q54;
            {var subQ0=sQuery(id+"F0.wireOp",EDGE,"E12");var subQ1=makeQuery(id+"F0.imprint","INTERSECT",VERTEX,{"derivedFrom":[sQuery(id+"F0.wireOp",EDGE,"E2"),subQ0]});Q54=makeQuery(id+"F0.imprint","IMPRINT",FACE,{"disambiguationData":[TD([[makeQuery(id+"F0.imprint","IMPRINT",EDGE,{"disambiguationData":[TD([[subQ1,1.0]])],"derivedFrom":subQ0}),1.0]])]});}
            var Q55;
            {var subQ0=sQuery(id+"F0.wireOp",EDGE,"E85");var subQ1=sQuery(id+"F0.wireOp",EDGE,"E33");var subQ2=makeQuery(id+"F0.imprint","INTERSECT",VERTEX,{"derivedFrom":[subQ1,subQ0]});Q55=makeQuery(id+"F0.imprint","IMPRINT",FACE,{"disambiguationData":[TD([[makeQuery(id+"F0.imprint","IMPRINT",EDGE,{"disambiguationData":[TD([[subQ2,-1.0]])],"derivedFrom":subQ1}),-1.0]])]});}
            var Q56;
            {var subQ0=sQuery(id+"F0.wireOp",EDGE,"E84");var subQ1=sQuery(id+"F0.wireOp",EDGE,"E2");var subQ2=makeQuery(id+"F0.imprint","INTERSECT",VERTEX,{"derivedFrom":[subQ1,subQ0]});Q56=makeQuery(id+"F0.imprint","IMPRINT",FACE,{"disambiguationData":[TD([[makeQuery(id+"F0.imprint","IMPRINT",EDGE,{"disambiguationData":[TD([[subQ2,-1.0]])],"derivedFrom":subQ1}),1.0]])]});}
            var Q57;
            {var subQ0=sQuery(id+"F0.wireOp",EDGE,"E5");var subQ1=makeQuery(id+"F0.imprint","INTERSECT",VERTEX,{"derivedFrom":[subQ0,sQuery(id+"F0.wireOp",EDGE,"E27.MirrorCS")]});Q57=makeQuery(id+"F0.imprint","IMPRINT",FACE,{"disambiguationData":[TD([[makeQuery(id+"F0.imprint","IMPRINT",EDGE,{"disambiguationData":[TD([[subQ1,1.0]])],"derivedFrom":subQ0}),-1.0]])]});}
            var Q58;
            {var subQ0=sQuery(id+"F0.wireOp",EDGE,"E13");var subQ1=sQuery(id+"F0.wireOp",EDGE,"E2");var subQ2=makeQuery(id+"F0.imprint","INTERSECT",VERTEX,{"derivedFrom":[subQ1,subQ0]});Q58=makeQuery(id+"F0.imprint","IMPRINT",FACE,{"disambiguationData":[TD([[makeQuery(id+"F0.imprint","IMPRINT",EDGE,{"disambiguationData":[TD([[subQ2,1.0]])],"derivedFrom":subQ1}),1.0]])]});}
            var Q59;
            {var subQ0=sQuery(id+"F0.wireOp",EDGE,"E33");var subQ1=sQuery(id+"F0.wireOp",EDGE,"E13");var subQ2=makeQuery(id+"F0.imprint","INTERSECT",VERTEX,{"derivedFrom":[subQ1,subQ0]});Q59=makeQuery(id+"F0.imprint","IMPRINT",FACE,{"disambiguationData":[TD([[makeQuery(id+"F0.imprint","IMPRINT",EDGE,{"disambiguationData":[TD([[subQ2,1.0]])],"derivedFrom":subQ1}),1.0]])]});}
            extrude(context, id + "F1", {"entities" : qUnion([Q0, Q1, Q2, Q3, Q4, Q5, Q6, Q7, Q8, Q9, Q10, Q11, Q12, Q13, Q14, Q15, Q16, Q17, Q18, Q19, Q20, Q21, Q22, Q23, Q24, Q25, Q26, Q27, Q28, Q29, Q30, Q31, Q32, Q33, Q34, Q35, Q36, Q37, Q38, Q39, Q40, Q41, Q42, Q43, Q44, Q45, Q46, Q47, Q48, Q49, Q50, Q51, Q52, Q53, Q54, Q55, Q56, Q57, Q58, Q59]), "oppositeDirection" : true, "depth" : 1.5 * mm});
        }
    });
